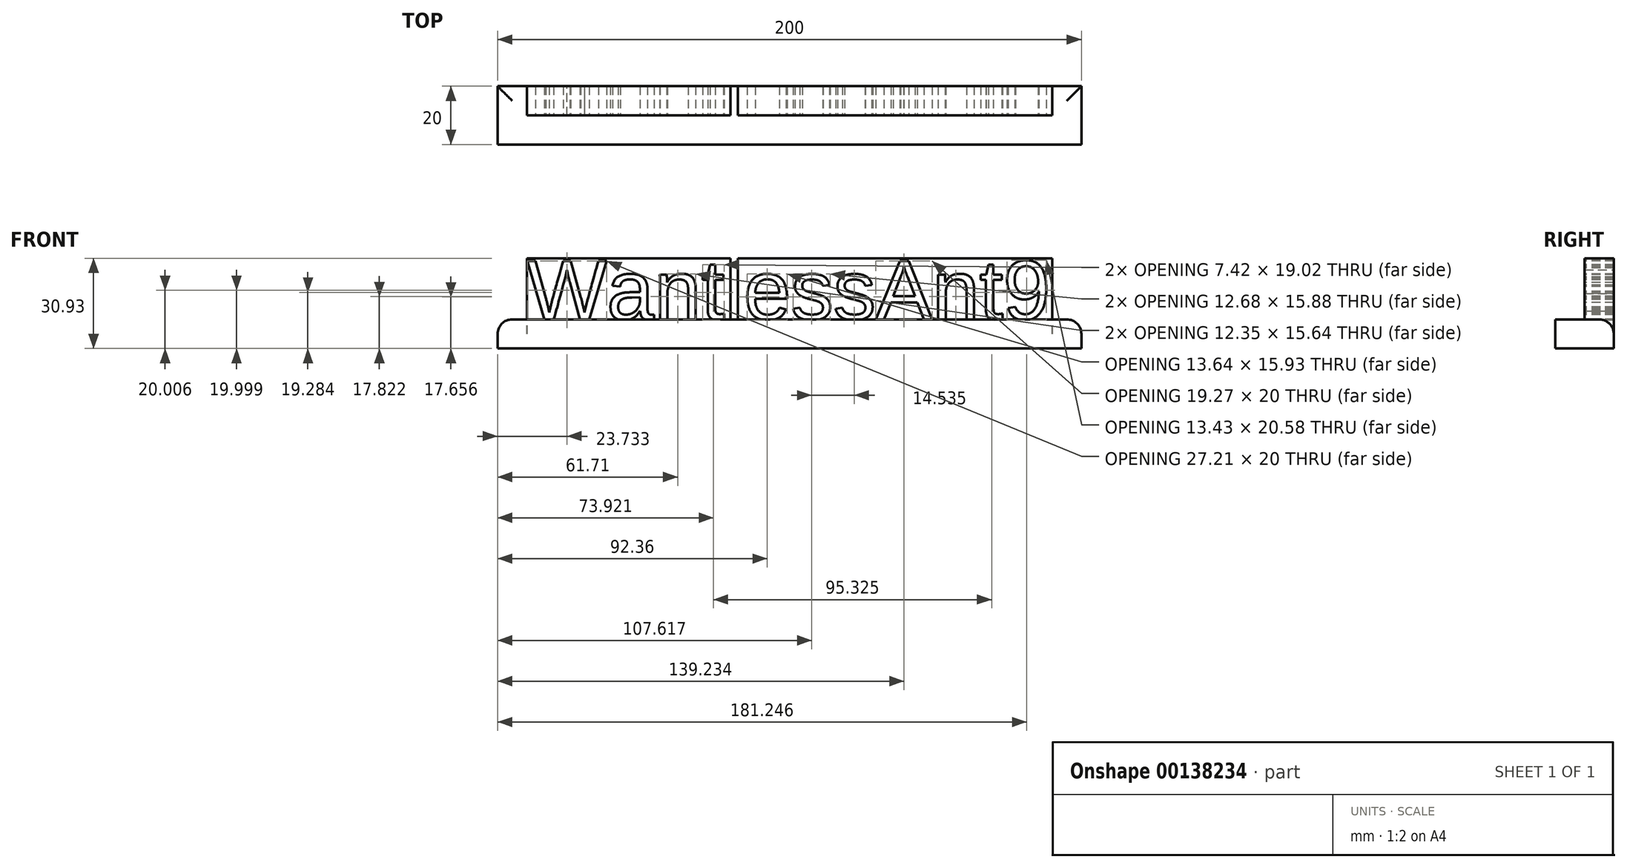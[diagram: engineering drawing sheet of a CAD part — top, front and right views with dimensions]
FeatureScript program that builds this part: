
annotation { "Feature Type Name" : "Feature", "Feature Type Description" : "" }
export const myFeature = defineFeature(function(context is Context, id is Id, definition is map)
    precondition{}
    {
        {
            var Q0;
            Q0=qCreatedBy(makeId("Top.planeOp"),FACE);
            var sketch = newSketch(context, id + "F0", { "sketchPlane" : qUnion([Q0])});
            skLineSegment(sketch, "E0", {"start": v(0, 10) * mm, "end": v(-100, 10) * mm});
            skLineSegment(sketch, "E1", {"start": v(0, 10) * mm, "end": v(100, 10) * mm});
            skLineSegment(sketch, "E2", {"start": v(-100, 10) * mm, "end": v(-100, -20) * mm});
            skLineSegment(sketch, "E3", {"start": v(-100, -20) * mm, "end": v(100, -20) * mm});
            skLineSegment(sketch, "E4", {"start": v(100, -20) * mm, "end": v(100, 10) * mm});
            skSolve(sketch);
        }
        {
            var Q0;
            Q0 = qSketchRegion(id + "F0", true);
            extrude(context, id + "F1", {"entities" : qUnion([Q0]), "depth" : 10 * mm});
        }
        {
            var Q0;
            Q0=makeQuery(id+"F1.opExtrude","CAP_FACE",FACE,{"disambiguationData":[OSD([sQuery(id+"F0.wireOp",EDGE,"E0"),sQuery(id+"F0.wireOp",EDGE,"E1"),sQuery(id+"F0.wireOp",EDGE,"E2"),sQuery(id+"F0.wireOp",EDGE,"E3"),sQuery(id+"F0.wireOp",EDGE,"E4")])],"isStart":false});
            var sketch = newSketch(context, id + "F2", { "sketchPlane" : qUnion([Q0])});
            skLineSegment(sketch, "E5", {"start": v(-100, 10) * mm, "end": v(-90, 10) * mm});
            skLineSegment(sketch, "E6", {"start": v(100, 10) * mm, "end": v(90, 10) * mm});
            skLineSegment(sketch, "E7", {"start": v(-90, 10) * mm, "end": v(-90, 0) * mm});
            skLineSegment(sketch, "E8", {"start": v(90, 10) * mm, "end": v(90, 0) * mm});
            skLineSegment(sketch, "E9", {"start": v(-90, 0) * mm, "end": v(90, 0) * mm});
            skLineSegment(sketch, "E10", {"start": v(-90, 10) * mm, "end": v(90, 10) * mm});
            skSolve(sketch);
        }
        {
            var Q0;
            Q0=makeQuery(id+"F2.imprint","IMPRINT",FACE,{"disambiguationData":[TD([[makeQuery(id+"F2.imprint","IMPRINT",EDGE,{"derivedFrom":sQuery(id+"F2.wireOp",EDGE,"E7")}),1.0]])]});
            extrude(context, id + "F3", {"entities" : qUnion([Q0]), "operationType" : NewBodyOperationType.ADD, "depth" : 20.93 * mm});
        }
        {
            var Q0;
            Q0=makeQuery(id+"F3.opExtrude","SWEPT_FACE",FACE,{"disambiguationData":[OSD([sQuery(id+"F2.wireOp",EDGE,"E9")])]});
            var sketch = newSketch(context, id + "F4", { "sketchPlane" : qUnion([Q0])});
            skText(sketch, "E11", { "text": "WantlessAnt9", "fontName": "Arimo-Regular.ttf"});
            const initialGuessF4  = {"E11": [-0.09, 0.01, 1, 0, 0.02093]};
            skSetInitialGuess(sketch, initialGuessF4);
            skSolve(sketch);
        }
        {
            var Q0;
            Q0=makeQuery(id+"F1.opExtrude","SWEPT_FACE",FACE,{"disambiguationData":[OSD([sQuery(id+"F0.wireOp",EDGE,"E3")])]});
            extrude(context, id + "F5", {"entities" : qUnion([Q0]), "operationType" : NewBodyOperationType.REMOVE, "oppositeDirection" : true, "depth" : 10 * mm});
        }
        {
            var Q0;
            Q0=makeQuery(id+"F1.opExtrude","CAP_EDGE",EDGE,{"disambiguationData":[OSD([sQuery(id+"F0.wireOp",EDGE,"E2")])],"isStart":false});
            var Q1;
            {var subQ0=sQuery(id+"F0.wireOp",EDGE,"E3");Q1=makeQuery(id+"F5.boolean.opBoolean","COPY",EDGE,{"derivedFrom":makeQuery(id+"F5.opExtrude","CAP_EDGE",EDGE,{"disambiguationData":[OSD([subQ0]),TDD([makeQuery(id+"F1.opExtrude","CAP_EDGE",EDGE,{"disambiguationData":[OSD([subQ0])],"isStart":false})])],"isStart":false})});}
            var Q2;
            Q2=makeQuery(id+"F1.opExtrude","CAP_EDGE",EDGE,{"disambiguationData":[OSD([sQuery(id+"F0.wireOp",EDGE,"E4")])],"isStart":false});
            var Q3;
            {var subQ0=sQuery(id+"F0.wireOp",EDGE,"E4");var subQ1=sQuery(id+"F0.wireOp",EDGE,"E1");var subQ2=sQuery(id+"F0.wireOp",EDGE,"E0");Q3=makeQuery(id+"F3.boolean.opBoolean","SPLIT",EDGE,{"disambiguationData":[TD([makeQuery(id+"F1.opExtrude","SWEPT_FACE",FACE,{"disambiguationData":[OSD([subQ0])]})])],"derivedFrom":makeQuery(id+"F1.opExtrude","CAP_EDGE",EDGE,{"disambiguationData":[OSD([subQ2,subQ1])],"isStart":false})});}
            var Q4;
            {var subQ0=sQuery(id+"F0.wireOp",EDGE,"E2");var subQ1=sQuery(id+"F0.wireOp",EDGE,"E1");var subQ2=sQuery(id+"F0.wireOp",EDGE,"E0");Q4=makeQuery(id+"F3.boolean.opBoolean","SPLIT",EDGE,{"disambiguationData":[TD([makeQuery(id+"F1.opExtrude","SWEPT_FACE",FACE,{"disambiguationData":[OSD([subQ0])]})])],"derivedFrom":makeQuery(id+"F1.opExtrude","CAP_EDGE",EDGE,{"disambiguationData":[OSD([subQ2,subQ1])],"isStart":false})});}
            fillet(context, id + "F6", {"entities" : qUnion([Q0, Q1, Q2, Q3, Q4]), "radius" : 5 * mm, "tangentPropagation" : true, "allowEdgeOverflow" : false});
        }
        {
            var Q0;
            Q0=makeQuery(id+"F1.opExtrude","SWEPT_BODY",BODY,{"disambiguationData":[OSD([sQuery(id+"F0.wireOp",EDGE,"E0"),sQuery(id+"F0.wireOp",EDGE,"E1"),sQuery(id+"F0.wireOp",EDGE,"E2"),sQuery(id+"F0.wireOp",EDGE,"E3"),sQuery(id+"F0.wireOp",EDGE,"E4")])]});
            transform(context, id + "F7", {"entities" : qUnion([Q0]), "transformType" : TransformType.TRANSLATION_3D, "dx" : 0 * mm, "dy" : 0 * mm, "dz" : 0 * mm, "makeCopy" : true});
        }
        {
            var Q0;
            Q0 = qSketchRegion(id + "F4", true);
            extrude(context, id + "F8", {"entities" : qUnion([Q0]), "operationType" : NewBodyOperationType.REMOVE, "oppositeDirection" : true, "depth" : 10 * mm});
        }
    });
